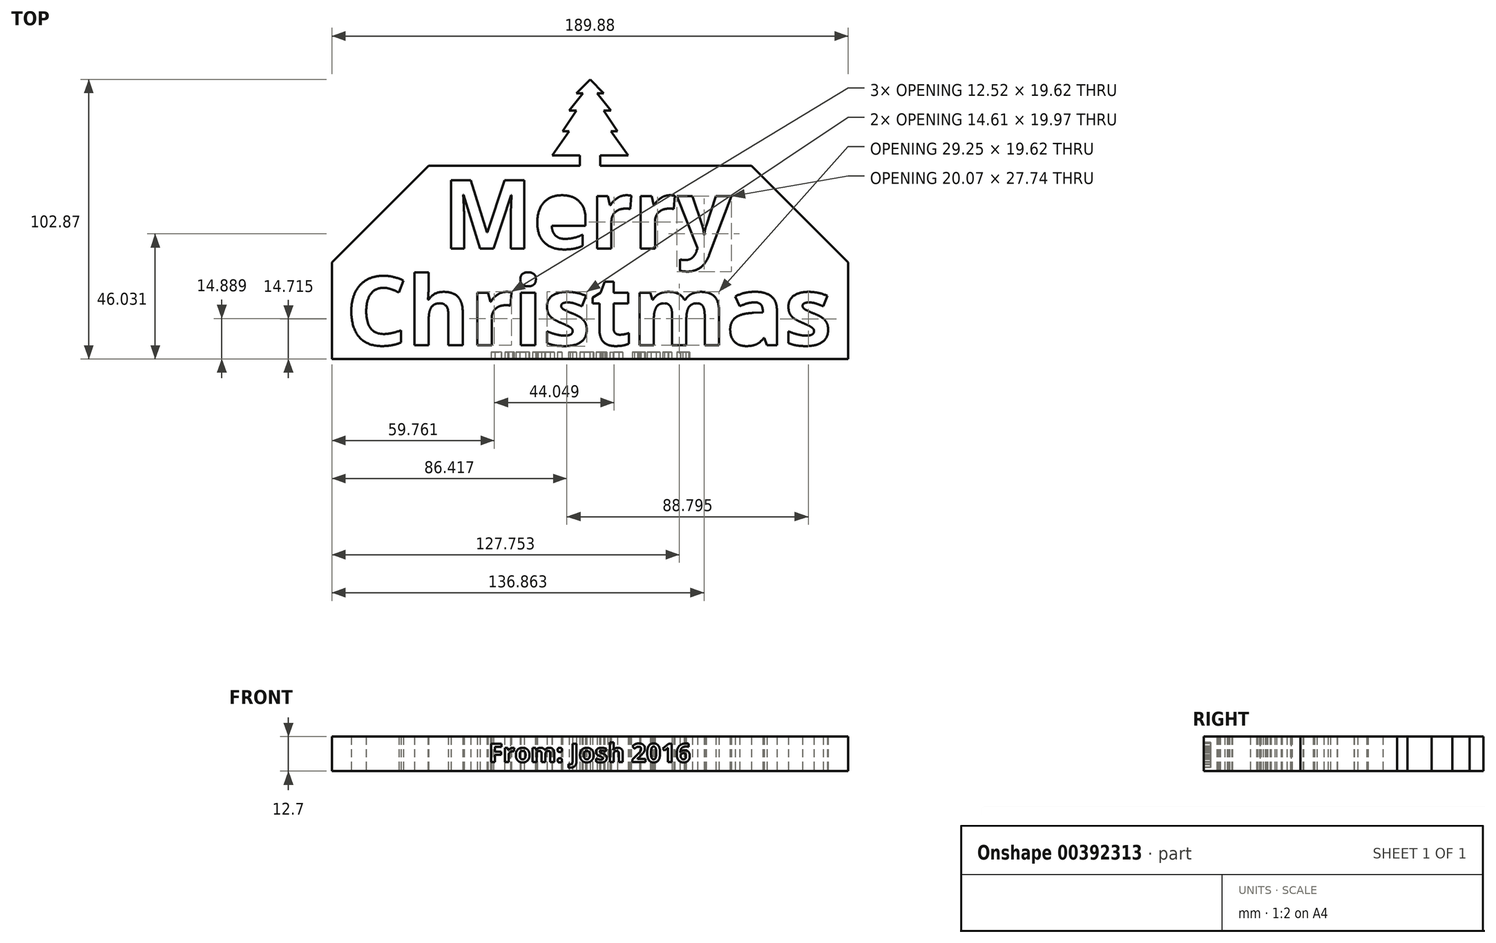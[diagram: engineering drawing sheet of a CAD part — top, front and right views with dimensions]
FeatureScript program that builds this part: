
annotation { "Feature Type Name" : "Feature", "Feature Type Description" : "" }
export const myFeature = defineFeature(function(context is Context, id is Id, definition is map)
    precondition{}
    {
        {
            var Q0;
            Q0=qCreatedBy(makeId("Top.planeOp"),FACE);
            var sketch = newSketch(context, id + "F0", { "sketchPlane" : qUnion([Q0])});
            skText(sketch, "E0", { "text": "Merry", "fontName": "OpenSans-Bold.ttf"});
            skText(sketch, "E1", { "text": "Christmas", "fontName": "OpenSans-Bold.ttf"});
            skLineSegment(sketch, "E2.bottom", {"start": v(-59.33, 35.56) * mm, "end": v(59.33, 35.56) * mm});
            skLineSegment(sketch, "E2.top", {"start": v(-94.94, -35.56) * mm, "end": v(94.94, -35.56) * mm});
            skLineSegment(sketch, "E2.left", {"start": v(-94.94, 0) * mm, "end": v(-94.94, -35.56) * mm});
            skLineSegment(sketch, "E2.right", {"start": v(94.94, 0) * mm, "end": v(94.94, -35.56) * mm});
            skLineSegment(sketch, "E3", {"start": v(-59.33, 35.56) * mm, "end": v(-94.94, 0) * mm});
            skLineSegment(sketch, "E4", {"start": v(59.33, 35.56) * mm, "end": v(94.94, 0) * mm});
            skPoint(sketch, "E5.orphan", {"position": v(-94.94, 35.56) * mm});
            skLineSegment(sketch, "E6", {"start": v(3.81, 35.56) * mm, "end": v(3.81, 39.37) * mm});
            skLineSegment(sketch, "E7", {"start": v(3.81, 39.37) * mm, "end": v(13.97, 39.37) * mm});
            skLineSegment(sketch, "E8", {"start": v(13.97, 39.37) * mm, "end": v(7.62, 48.26) * mm});
            skLineSegment(sketch, "E9", {"start": v(7.62, 48.26) * mm, "end": v(10.16, 48.26) * mm});
            skLineSegment(sketch, "E10", {"start": v(10.16, 48.26) * mm, "end": v(5.08, 55.88) * mm});
            skLineSegment(sketch, "E11", {"start": v(5.08, 55.88) * mm, "end": v(7.62, 55.88) * mm});
            skLineSegment(sketch, "E12", {"start": v(7.62, 55.88) * mm, "end": v(2.54, 62.23) * mm});
            skLineSegment(sketch, "E13", {"start": v(2.54, 62.23) * mm, "end": v(5.08, 62.23) * mm});
            skLineSegment(sketch, "E14", {"start": v(5.08, 62.23) * mm, "end": v(0, 67.31) * mm});
            skLineSegment(sketch, "E15.MirrorCS", {"start": v(-5.08, 62.23) * mm, "end": v(0, 67.31) * mm});
            skLineSegment(sketch, "E16.MirrorCS", {"start": v(-2.54, 62.23) * mm, "end": v(-5.08, 62.23) * mm});
            skLineSegment(sketch, "E17.MirrorCS", {"start": v(-7.62, 55.88) * mm, "end": v(-2.54, 62.23) * mm});
            skLineSegment(sketch, "E18.MirrorCS", {"start": v(-5.08, 55.88) * mm, "end": v(-7.62, 55.88) * mm});
            skLineSegment(sketch, "E19.MirrorCS", {"start": v(-10.16, 48.26) * mm, "end": v(-5.08, 55.88) * mm});
            skLineSegment(sketch, "E20.MirrorCS", {"start": v(-7.62, 48.26) * mm, "end": v(-10.16, 48.26) * mm});
            skLineSegment(sketch, "E21.MirrorCS", {"start": v(-13.97, 39.37) * mm, "end": v(-7.62, 48.26) * mm});
            skLineSegment(sketch, "E22.MirrorCS", {"start": v(-3.81, 39.37) * mm, "end": v(-13.97, 39.37) * mm});
            skLineSegment(sketch, "E23.MirrorCS", {"start": v(-3.81, 35.56) * mm, "end": v(-3.81, 39.37) * mm});
            const initialGuessF0  = {"E0": [-0.05425, 0.00508, 1, 0, 0.0254], "E1": [-0.08986, -0.03048, 1, 0, 0.0254]};
            skSetInitialGuess(sketch, initialGuessF0);
            skSolve(sketch);
        }
        {
            var Q0;
            Q0 = qSketchRegion(id + "F0", true);
            extrude(context, id + "F1", {"entities" : qUnion([Q0]), "depth" : 12.7 * mm});
        }
        {
            var Q0;
            Q0=makeQuery(id+"F1.opExtrude","SWEPT_FACE",FACE,{"disambiguationData":[OSD([sQuery(id+"F0.wireOp",EDGE,"E2.top")])]});
            var sketch = newSketch(context, id + "F2", { "sketchPlane" : qUnion([Q0])});
            skText(sketch, "E24", { "text": "From: Josh 2016", "fontName": "OpenSans-Bold.ttf"});
            const initialGuessF2  = {"E24": [-0.03729, 0.0033, 1, 0, 0.00686]};
            skSetInitialGuess(sketch, initialGuessF2);
            skSolve(sketch);
        }
        {
            var Q0;
            Q0 = qSketchRegion(id + "F2", true);
            extrude(context, id + "F3", {"entities" : qUnion([Q0]), "operationType" : NewBodyOperationType.REMOVE, "oppositeDirection" : true, "depth" : 2.54 * mm});
        }
    });
